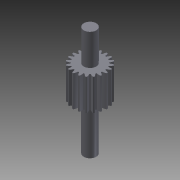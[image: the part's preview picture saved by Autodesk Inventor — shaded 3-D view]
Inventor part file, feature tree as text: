
AUTODESK INVENTOR PART (.ipt)
format: ipt  version: 2011 (Build 150239000, 239)  size: 224,256 bytes
history: native  units: mm (DEFAULTED — no unit token found)
features: sketch x4, extrude x3, plane x3, other x3
ambient origin geometry x8: Origin, YZ Plane, XZ Plane, XY Plane, X Axis, Y Axis, Z Axis, Center Point
bodies: Solid1 (feature_tree)
feature tree (13):
  extrude  "Extrusion1"  Depth=5.0mm TaperAngle=0.0deg
  plane  "Work Plane2"
  plane  "Work Plane8"
  plane  "Work Plane9"
  other  "Spur Gear"
  extrude  "Extrusion2"  Depth=10.0mm TaperAngle=0.0deg
  extrude  "Extrusion4"  Depth=1.570796mm TaperAngle=0.0deg
  sketch  "Sketch1"  dims[d0=5.5mm d1=5.0mm d2=0.0mm]
  sketch  "Sketch2"  dims[d3=5.0mm d4=10.0mm d5=0.0mm]
  other  "Srf1"
  sketch  "Sketch3"  dims[d16=10.0mm d17=0.0mm d34=1.570796mm]
  sketch  "Sketch5"  dims[d39=0.0mm d41=0.0mm d43=10.0mm d46=10.0mm d47=0.0mm d48=0.0mm d49=2.0mm d50=5.0mm d51=0.0mm d54=7.5mm d55=0.0mm]
  other  "Pitch Diameter"
